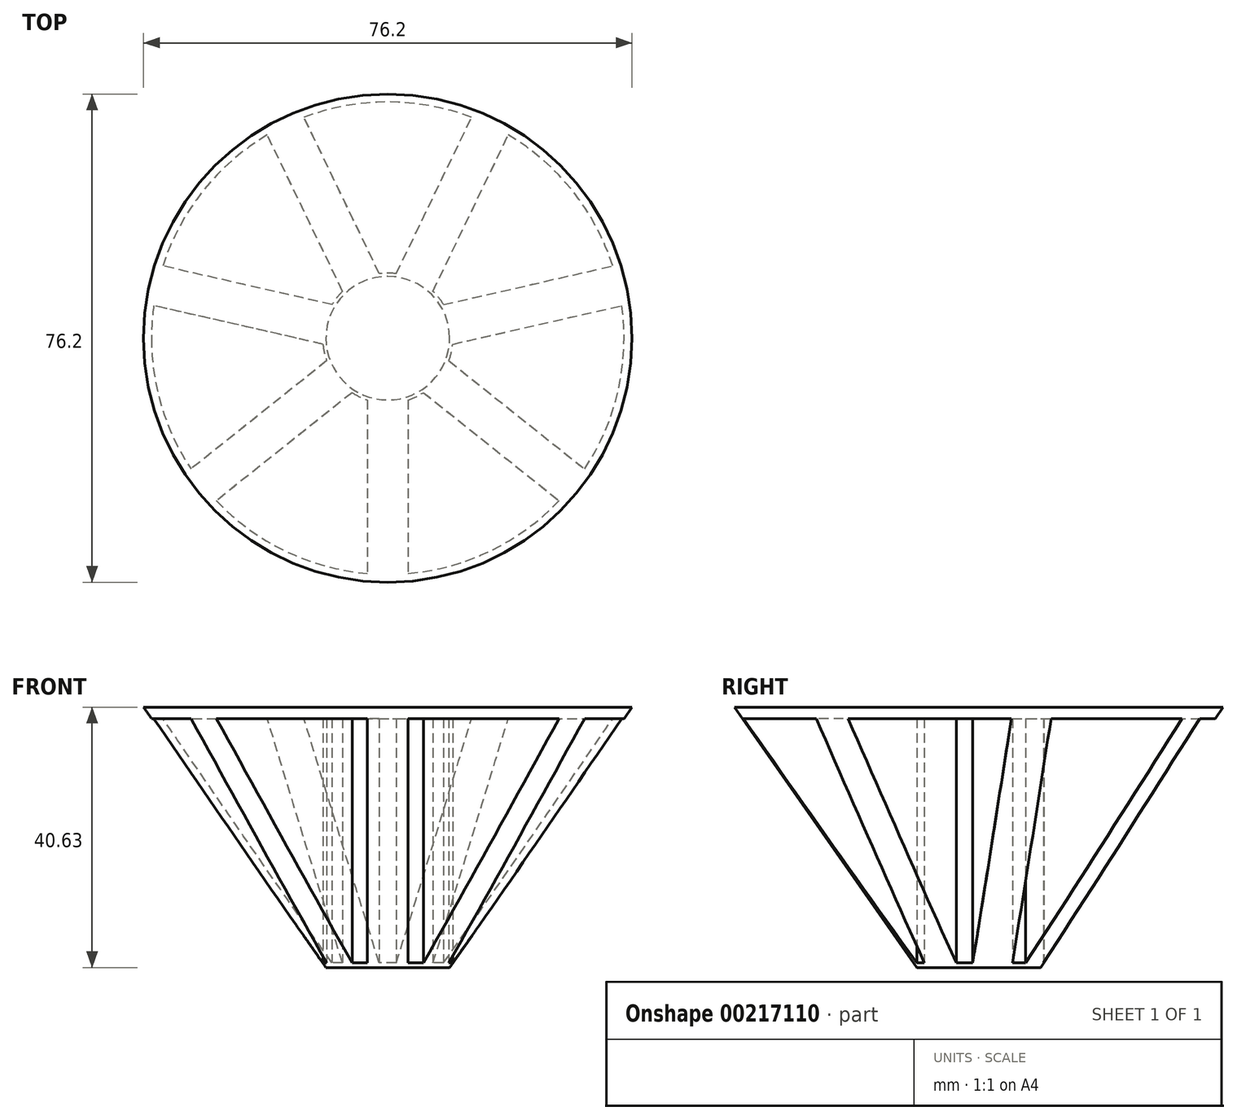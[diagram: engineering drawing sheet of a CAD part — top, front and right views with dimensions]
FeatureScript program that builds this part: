
annotation { "Feature Type Name" : "Feature", "Feature Type Description" : "" }
export const myFeature = defineFeature(function(context is Context, id is Id, definition is map)
    precondition{}
    {
        {
            var Q0;
            Q0=qCreatedBy(makeId("Right.planeOp"),FACE);
            var sketch = newSketch(context, id + "F0", { "sketchPlane" : qUnion([Q0])});
            skLineSegment(sketch, "E0", {"start": v(0, 0) * mm, "end": v(-28.45, 40.63) * mm});
            skLineSegment(sketch, "E1", {"start": v(0, 0) * mm, "end": v(19.3, 0) * mm});
            skLineSegment(sketch, "E2.MirrorCS", {"start": v(19.3, 0) * mm, "end": v(47.75, 40.63) * mm});
            skLineSegment(sketch, "E3", {"start": v(-28.45, 40.63) * mm, "end": v(47.75, 40.63) * mm});
            skPoint(sketch, "E4.start.orphan", {"position": v(9.65, 0) * mm});
            skLineSegment(sketch, "E5", {"start": v(9.65, 0) * mm, "end": v(9.65, 40.63) * mm});
            skSolve(sketch);
        }
        {
            var Q0;
            {var subQ0=sQuery(id+"F0.wireOp",EDGE,"E0");Q0=makeQuery(id+"F0.imprint","IMPRINT",FACE,{"disambiguationData":[TD([[makeQuery(id+"F0.imprint","IMPRINT",EDGE,{"derivedFrom":subQ0}),-1.0]])]});}
            var Q1;
            Q1=sQuery(id+"F0.wireOp",EDGE,"E5");
            revolve(context, id + "F1", {"entities" : qUnion([Q0]), "axis" : qUnion([Q1]), "revolveType" : RevolveType.FULL});
        }
        {
            var Q0;
            Q0=makeQuery(id+"F1.opRevolve","SWEPT_FACE",FACE,{"disambiguationData":[OSD([sQuery(id+"F0.wireOp",EDGE,"E1")])]});
            var sketch = newSketch(context, id + "F2", { "sketchPlane" : qUnion([Q0])});
            skCircle(sketch, "E6", {"center": v(0, -9.65) * mm, "radius": 10.16 * mm});
            skCircle(sketch, "E7", {"center": v(0, -9.65) * mm, "radius": 38.44 * mm});
            skLineSegment(sketch, "E8", {"start": v(0, 0) * mm, "end": v(0, 0.5) * mm});
            skLineSegment(sketch, "E9.0", {"start": v(3.18, 0) * mm, "end": v(3.18, 28.8) * mm});
            skLineSegment(sketch, "E10.0", {"start": v(-3.18, 0) * mm, "end": v(-3.18, 28.8) * mm});
            skLineSegment(sketch, "E11.1.0", {"start": v(-5.56, -1.15) * mm, "end": v(-28.07, 16.8) * mm});
            skLineSegment(sketch, "E11.1.1", {"start": v(-9.52, -6.11) * mm, "end": v(-32.03, 11.84) * mm});
            skLineSegment(sketch, "E11.2.0", {"start": v(-10.11, -8.7) * mm, "end": v(-38.18, -15.1) * mm});
            skLineSegment(sketch, "E11.2.1", {"start": v(-8.7, -14.9) * mm, "end": v(-36.77, -21.3) * mm});
            skLineSegment(sketch, "E11.3.0", {"start": v(-7.05, -16.96) * mm, "end": v(-19.54, -42.9) * mm});
            skLineSegment(sketch, "E11.3.1", {"start": v(-1.33, -19.72) * mm, "end": v(-13.82, -45.66) * mm});
            skLineSegment(sketch, "E11.4.0", {"start": v(1.33, -19.72) * mm, "end": v(13.82, -45.66) * mm});
            skLineSegment(sketch, "E11.4.1", {"start": v(7.05, -16.96) * mm, "end": v(19.54, -42.9) * mm});
            skLineSegment(sketch, "E11.5.0", {"start": v(8.7, -14.9) * mm, "end": v(36.77, -21.3) * mm});
            skLineSegment(sketch, "E11.5.1", {"start": v(10.11, -8.7) * mm, "end": v(38.18, -15.1) * mm});
            skLineSegment(sketch, "E11.6.0", {"start": v(9.52, -6.11) * mm, "end": v(32.03, 11.84) * mm});
            skLineSegment(sketch, "E11.6.1", {"start": v(5.56, -1.15) * mm, "end": v(28.07, 16.8) * mm});
            skSolve(sketch);
        }
        {
            var Q0;
            {var subQ0=sQuery(id+"F2.wireOp",EDGE,"E10.0");var subQ1=sQuery(id+"F2.wireOp",EDGE,"E6");var subQ2=makeQuery(id+"F2.imprint","INTERSECT",VERTEX,{"derivedFrom":[subQ1,subQ0]});Q0=makeQuery(id+"F2.imprint","IMPRINT",FACE,{"disambiguationData":[TD([[makeQuery(id+"F2.imprint","IMPRINT",EDGE,{"disambiguationData":[TD([[subQ2,-1.0]])],"derivedFrom":subQ1}),-1.0]])]});}
            var Q1;
            {var subQ0=sQuery(id+"F2.wireOp",EDGE,"E9.0");var subQ1=sQuery(id+"F2.wireOp",EDGE,"E6");var subQ2=makeQuery(id+"F2.imprint","INTERSECT",VERTEX,{"derivedFrom":[subQ1,subQ0]});Q1=makeQuery(id+"F2.imprint","IMPRINT",FACE,{"disambiguationData":[TD([[makeQuery(id+"F2.imprint","IMPRINT",EDGE,{"disambiguationData":[TD([[subQ2,1.0]])],"derivedFrom":subQ1}),-1.0]])]});}
            var Q2;
            {var subQ0=sQuery(id+"F2.wireOp",EDGE,"E11.5.1");var subQ1=sQuery(id+"F2.wireOp",EDGE,"E6");var subQ2=makeQuery(id+"F2.imprint","INTERSECT",VERTEX,{"derivedFrom":[subQ1,subQ0]});Q2=makeQuery(id+"F2.imprint","IMPRINT",FACE,{"disambiguationData":[TD([[makeQuery(id+"F2.imprint","IMPRINT",EDGE,{"disambiguationData":[TD([[subQ2,-1.0]])],"derivedFrom":subQ1}),-1.0]])]});}
            var Q3;
            {var subQ0=sQuery(id+"F2.wireOp",EDGE,"E11.4.1");var subQ1=sQuery(id+"F2.wireOp",EDGE,"E6");var subQ2=makeQuery(id+"F2.imprint","INTERSECT",VERTEX,{"derivedFrom":[subQ1,subQ0]});Q3=makeQuery(id+"F2.imprint","IMPRINT",FACE,{"disambiguationData":[TD([[makeQuery(id+"F2.imprint","IMPRINT",EDGE,{"disambiguationData":[TD([[subQ2,-1.0]])],"derivedFrom":subQ1}),-1.0]])]});}
            var Q4;
            {var subQ0=sQuery(id+"F2.wireOp",EDGE,"E11.3.1");var subQ1=sQuery(id+"F2.wireOp",EDGE,"E6");var subQ2=makeQuery(id+"F2.imprint","INTERSECT",VERTEX,{"derivedFrom":[subQ1,subQ0]});Q4=makeQuery(id+"F2.imprint","IMPRINT",FACE,{"disambiguationData":[TD([[makeQuery(id+"F2.imprint","IMPRINT",EDGE,{"disambiguationData":[TD([[subQ2,-1.0]])],"derivedFrom":subQ1}),-1.0]])]});}
            var Q5;
            {var subQ0=sQuery(id+"F2.wireOp",EDGE,"E11.2.1");var subQ1=sQuery(id+"F2.wireOp",EDGE,"E6");var subQ2=makeQuery(id+"F2.imprint","INTERSECT",VERTEX,{"derivedFrom":[subQ1,subQ0]});Q5=makeQuery(id+"F2.imprint","IMPRINT",FACE,{"disambiguationData":[TD([[makeQuery(id+"F2.imprint","IMPRINT",EDGE,{"disambiguationData":[TD([[subQ2,-1.0]])],"derivedFrom":subQ1}),-1.0]])]});}
            var Q6;
            {var subQ0=sQuery(id+"F2.wireOp",EDGE,"E11.1.1");var subQ1=sQuery(id+"F2.wireOp",EDGE,"E6");var subQ2=makeQuery(id+"F2.imprint","INTERSECT",VERTEX,{"derivedFrom":[subQ1,subQ0]});Q6=makeQuery(id+"F2.imprint","IMPRINT",FACE,{"disambiguationData":[TD([[makeQuery(id+"F2.imprint","IMPRINT",EDGE,{"disambiguationData":[TD([[subQ2,-1.0]])],"derivedFrom":subQ1}),-1.0]])]});}
            extrude(context, id + "F3", {"entities" : qUnion([Q0, Q1, Q2, Q3, Q4, Q5, Q6]), "operationType" : NewBodyOperationType.REMOVE, "oppositeDirection" : true, "depth" : 38.86 * mm});
        }
    });
